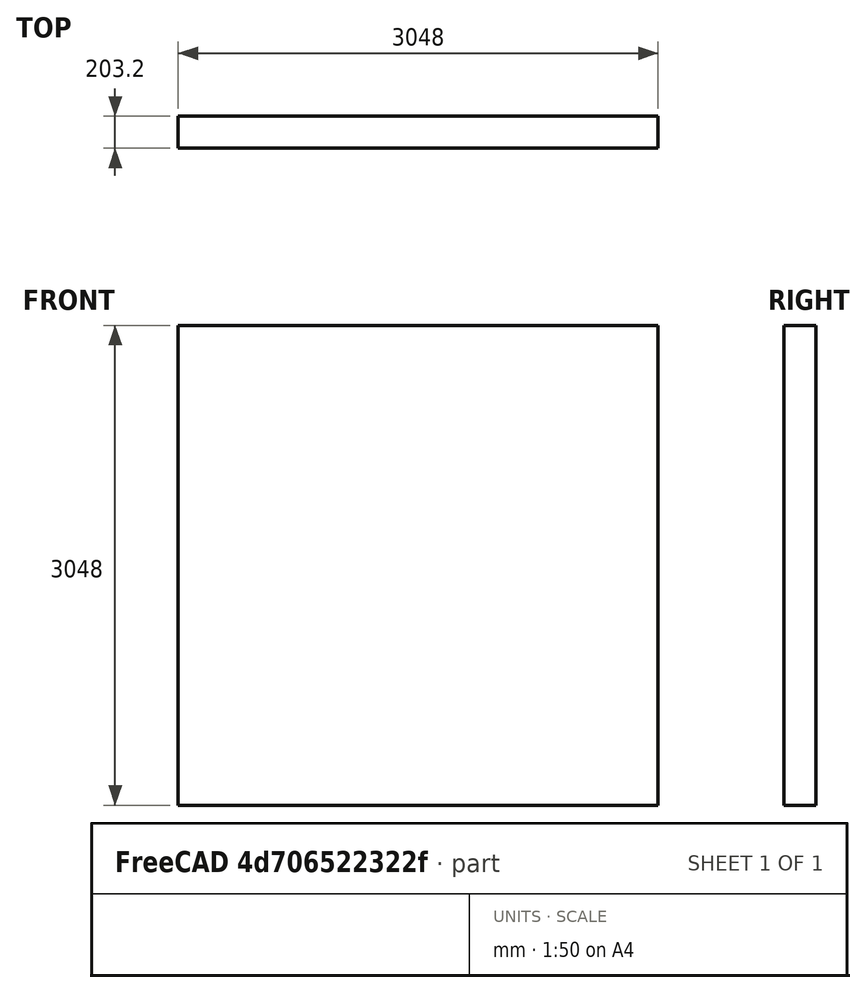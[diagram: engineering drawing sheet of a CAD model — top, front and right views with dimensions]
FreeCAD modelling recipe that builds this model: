
FCSTD DOCUMENT  (FreeCAD 0.17R8398 (Git))
Label: 3_Wall
License: CreativeCommons Attribution
LicenseURL: http://creativecommons.org/licenses/by/4.0/
objects: App::DocumentObjectGroupPython×4, Part::Feature×1, Part::Extrusion×1, Part::FeaturePython×1, App::MaterialObjectPython×1
note: 3 computed .brp shape members not serialized (recipe doc carries the construction recipe); baked Part::Feature solids carry a one-line shape summary decoded from their .brp

FEATURE [Part::Feature] Basic_Wall_Generic___8__149935_footprint
  shape: bbox 3049 x 203.8 x 0.6096 mm, 1 faces, 0 solids (baked)
FEATURE [Part::Extrusion] Basic_Wall_Generic___8__149935_body
  Base = -> Basic_Wall_Generic___8__149935_footprint
  Dir = (0,0,3048)
  DirMode = 0
  LengthFwd = 0
  LengthRev = 0
  Solid = false
  Symmetric = false
FEATURE [Part::FeaturePython] Basic_Wall_Generic___8__149935  label="Basic Wall:Generic - 8":149935"  # Arch/BIM object (typed FeaturePython)
  Align = 2
  Base = -> Basic_Wall_Generic___8__149935_body
  Face = 0
  Height = 2000
  HorizontalArea = 619354
  IfcAttributes = ExtendToStructure=IfcBoolean(.F.); IfcUID=38afGuERP8VQC9XMBPHSDG; IsExternal=IfcBoolean(.T.); LoadBearing=IfcBoolean(.F.); Reference=IfcIdentifier('Generic - 8"')
  Length = 0
  MoveWithHost = false
  Normal = (0,0,0)
  PerimeterLength = 6502.4
  Role = 0
  VerticalArea = 1.98193e+07
  Width = 200
FEATURE [App::DocumentObjectGroupPython] Level_1  label="Level 1"  # scripted group (container) (typed FeaturePython)
  Group = -> [Basic_Wall_Generic___8__149935]
  Height = 0
FEATURE [App::DocumentObjectGroupPython] Building  # scripted group (container) (typed FeaturePython)
  BuildingType = 0
  Group = -> [Level_1]
  Height = 0
FEATURE [App::DocumentObjectGroupPython] Default  # scripted group (container) (typed FeaturePython)
  Group = -> [Building]
  Height = 0
  Latitude = 0
  Longitude = 0
FEATURE [App::MaterialObjectPython] Default_Wall  label="Default Wall"  # material (typed FeaturePython)
FEATURE [App::DocumentObjectGroupPython] MaterialContainer  label="Materials"  # scripted group (container) (typed FeaturePython)
  Group = -> [Default_Wall]
